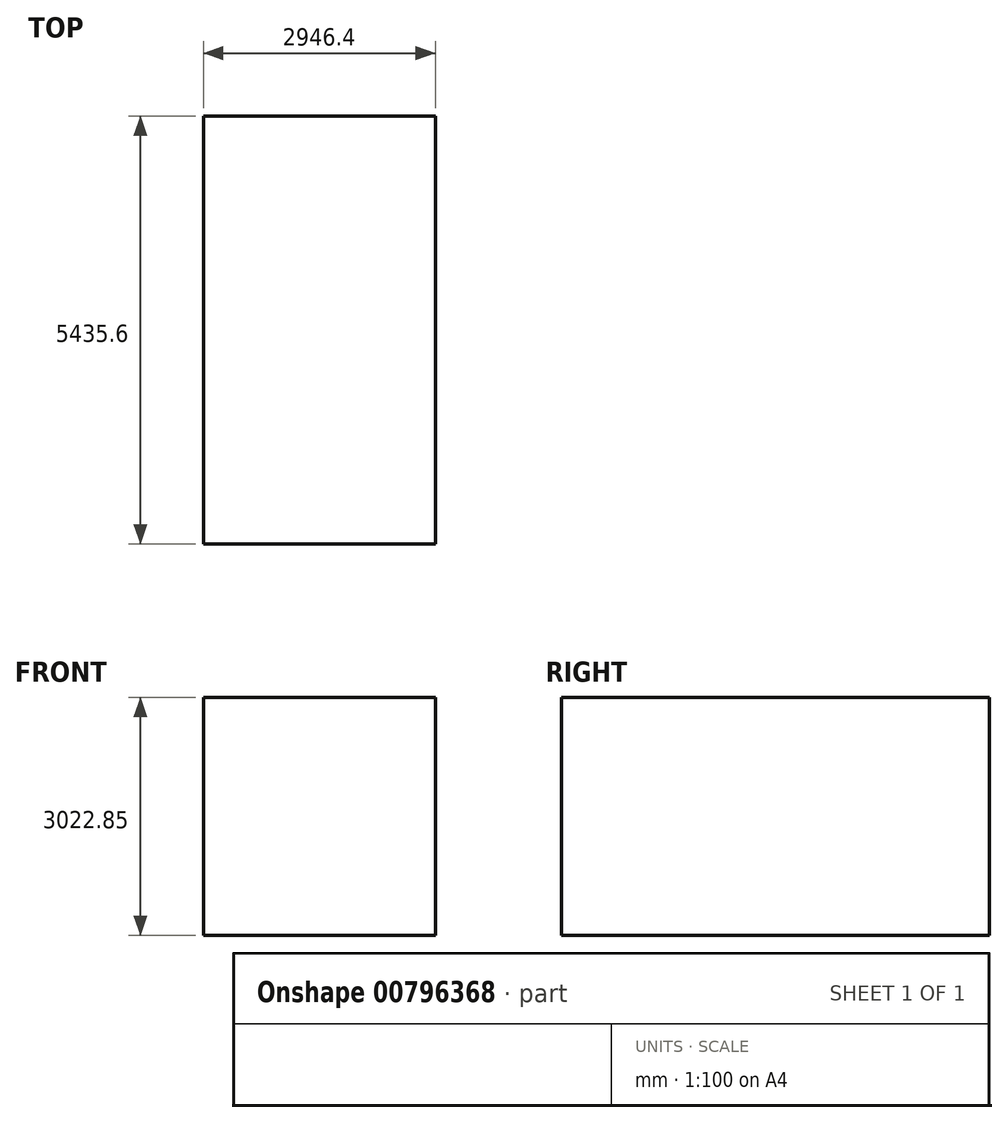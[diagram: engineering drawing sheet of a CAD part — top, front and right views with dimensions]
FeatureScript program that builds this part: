
annotation { "Feature Type Name" : "Feature", "Feature Type Description" : "" }
export const myFeature = defineFeature(function(context is Context, id is Id, definition is map)
    precondition{}
    {
        {
            var Q0;
            Q0=qCreatedBy(makeId("Top.planeOp"),FACE);
            var sketch = newSketch(context, id + "F0", { "sketchPlane" : qUnion([Q0])});
            skLineSegment(sketch, "E0.bottom", {"start": v(0, 0) * mm, "end": v(2946.4, 0) * mm});
            skLineSegment(sketch, "E0.top", {"start": v(0, -5435.6) * mm, "end": v(2946.4, -5435.6) * mm});
            skLineSegment(sketch, "E0.left", {"start": v(0, 0) * mm, "end": v(0, -5435.6) * mm});
            skLineSegment(sketch, "E0.right", {"start": v(2946.4, 0) * mm, "end": v(2946.4, -5435.6) * mm});
            skSolve(sketch);
        }
        {
            var Q0;
            Q0=makeQuery(id+"F0.imprint","IMPRINT",FACE,{"disambiguationData":[TD([[makeQuery(id+"F0.imprint","IMPRINT",EDGE,{"derivedFrom":sQuery(id+"F0.wireOp",EDGE,"E0.bottom")}),-1.0]])]});
            extrude(context, id + "F1", {"entities" : qUnion([Q0]), "depth" : 0.25 * mm, "offsetDistance" : 25.4 * mm});
        }
        {
            var Q0;
            Q0=makeQuery(id+"F1.opExtrude","CAP_FACE",FACE,{"disambiguationData":[OSD([sQuery(id+"F0.wireOp",EDGE,"E0.bottom"),sQuery(id+"F0.wireOp",EDGE,"E0.top"),sQuery(id+"F0.wireOp",EDGE,"E0.left"),sQuery(id+"F0.wireOp",EDGE,"E0.right")])],"isStart":false});
            var sketch = newSketch(context, id + "F2", { "sketchPlane" : qUnion([Q0])});
            skLineSegment(sketch, "E1", {"start": v(0, -5435.6) * mm, "end": v(0.25, -5435.6) * mm});
            skLineSegment(sketch, "E2", {"start": v(0.25, -5435.6) * mm, "end": v(0.25, -0.25) * mm});
            skLineSegment(sketch, "E3", {"start": v(0.25, -0.25) * mm, "end": v(2946.15, -0.25) * mm});
            skLineSegment(sketch, "E4", {"start": v(2946.15, -0.25) * mm, "end": v(2946.15, -5435.6) * mm});
            skLineSegment(sketch, "E5", {"start": v(2946.15, -5435.6) * mm, "end": v(2946.4, -5435.6) * mm});
            skLineSegment(sketch, "E6", {"start": v(2946.4, -5435.6) * mm, "end": v(2946.4, 0) * mm});
            skLineSegment(sketch, "E7", {"start": v(2946.4, 0) * mm, "end": v(0, 0) * mm});
            skLineSegment(sketch, "E8", {"start": v(0, 0) * mm, "end": v(0, -5435.6) * mm});
            skSolve(sketch);
        }
        {
            var Q0;
            Q0 = qSketchRegion(id + "F2", true);
            extrude(context, id + "F3", {"entities" : qUnion([Q0]), "operationType" : NewBodyOperationType.ADD, "depth" : 3022.6 * mm, "offsetDistance" : 25.4 * mm});
        }
    });
